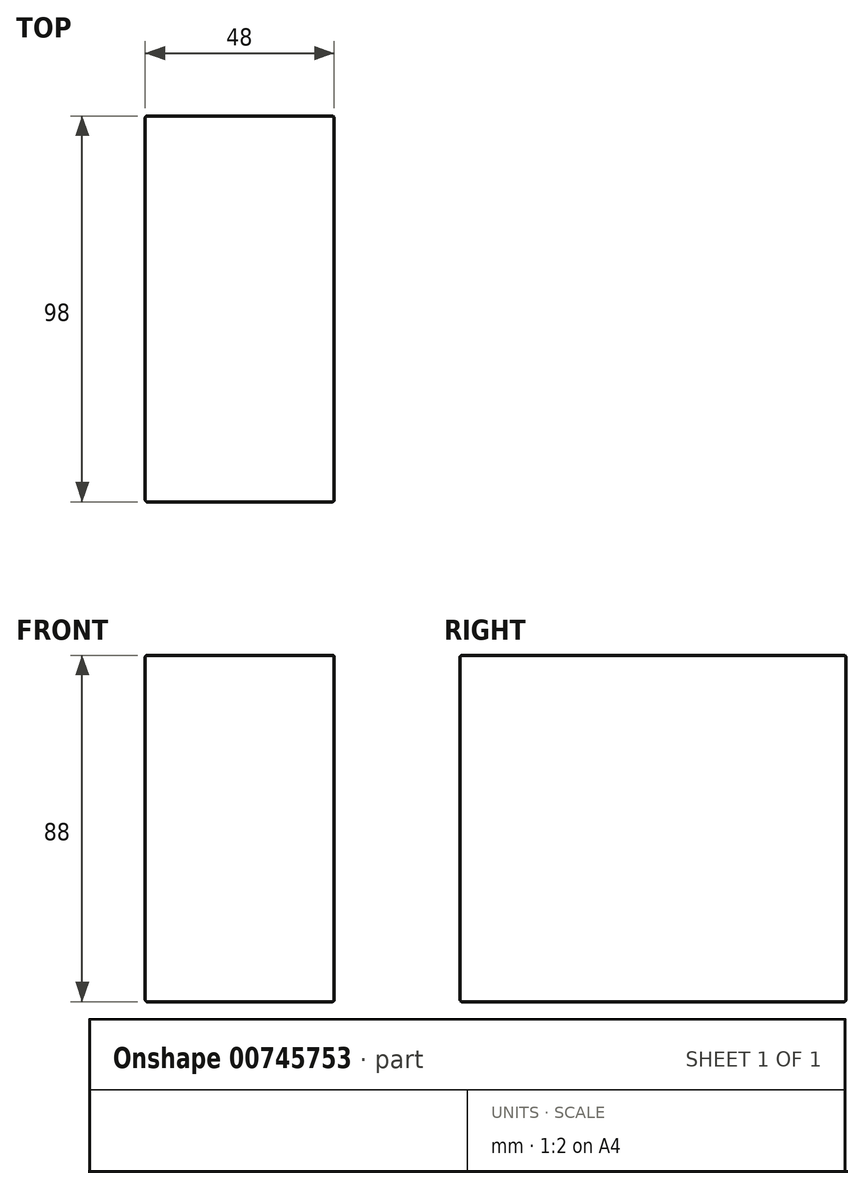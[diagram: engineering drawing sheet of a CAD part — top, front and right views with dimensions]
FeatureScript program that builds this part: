
annotation { "Feature Type Name" : "Feature", "Feature Type Description" : "" }
export const myFeature = defineFeature(function(context is Context, id is Id, definition is map)
    precondition{}
    {
        {
            var Q0;
            Q0=qCreatedBy(makeId("Front.planeOp"),FACE);
            var sketch = newSketch(context, id + "F0", { "sketchPlane" : qUnion([Q0])});
            skLineSegment(sketch, "E0.bottom", {"start": v(0, 0) * mm, "end": v(48, 0) * mm});
            skLineSegment(sketch, "E0.top", {"start": v(0, 88) * mm, "end": v(48, 88) * mm});
            skLineSegment(sketch, "E0.left", {"start": v(0, 0) * mm, "end": v(0, 88) * mm});
            skLineSegment(sketch, "E0.right", {"start": v(48, 0) * mm, "end": v(48, 88) * mm});
            skSolve(sketch);
        }
        {
            var Q0;
            Q0 = qSketchRegion(id + "F0", true);
            extrude(context, id + "F1", {"entities" : qUnion([Q0]), "oppositeDirection" : true, "depth" : 98 * mm, "offsetDistance" : 25 * mm});
        }
        {
            var Q0;
            Q0=makeQuery(id+"F1.opExtrude","CAP_EDGE",EDGE,{"disambiguationData":[OSD([sQuery(id+"F0.wireOp",EDGE,"E0.top")])],"isStart":true});
            var Q1;
            Q1=makeQuery(id+"F1.opExtrude","SWEPT_EDGE",EDGE,{"disambiguationData":[OSD([sQuery(id+"F0.wireOp",EDGE,"E0.top"),sQuery(id+"F0.wireOp",EDGE,"E0.right")])]});
            var Q2;
            Q2=makeQuery(id+"F1.opExtrude","CAP_EDGE",EDGE,{"disambiguationData":[OSD([sQuery(id+"F0.wireOp",EDGE,"E0.right")])],"isStart":true});
            var Q3;
            Q3=makeQuery(id+"F1.opExtrude","CAP_EDGE",EDGE,{"disambiguationData":[OSD([sQuery(id+"F0.wireOp",EDGE,"E0.left")])],"isStart":true});
            var Q4;
            Q4=makeQuery(id+"F1.opExtrude","SWEPT_EDGE",EDGE,{"disambiguationData":[OSD([sQuery(id+"F0.wireOp",EDGE,"E0.top"),sQuery(id+"F0.wireOp",EDGE,"E0.left")])]});
            var Q5;
            Q5=makeQuery(id+"F1.opExtrude","CAP_EDGE",EDGE,{"disambiguationData":[OSD([sQuery(id+"F0.wireOp",EDGE,"E0.top")])],"isStart":false});
            var Q6;
            Q6=makeQuery(id+"F1.opExtrude","CAP_EDGE",EDGE,{"disambiguationData":[OSD([sQuery(id+"F0.wireOp",EDGE,"E0.right")])],"isStart":false});
            var Q7;
            Q7=makeQuery(id+"F1.opExtrude","CAP_EDGE",EDGE,{"disambiguationData":[OSD([sQuery(id+"F0.wireOp",EDGE,"E0.left")])],"isStart":false});
            var Q8;
            Q8=makeQuery(id+"F1.opExtrude","SWEPT_EDGE",EDGE,{"disambiguationData":[OSD([sQuery(id+"F0.wireOp",EDGE,"E0.bottom"),sQuery(id+"F0.wireOp",EDGE,"E0.right")])]});
            var Q9;
            Q9=makeQuery(id+"F1.opExtrude","CAP_EDGE",EDGE,{"disambiguationData":[OSD([sQuery(id+"F0.wireOp",EDGE,"E0.bottom")])],"isStart":true});
            var Q10;
            Q10=makeQuery(id+"F1.opExtrude","CAP_EDGE",EDGE,{"disambiguationData":[OSD([sQuery(id+"F0.wireOp",EDGE,"E0.bottom")])],"isStart":false});
            var Q11;
            Q11=makeQuery(id+"F1.opExtrude","SWEPT_EDGE",EDGE,{"disambiguationData":[OSD([sQuery(id+"F0.wireOp",EDGE,"E0.bottom"),sQuery(id+"F0.wireOp",EDGE,"E0.left")])]});
            fillet(context, id + "F2", {"entities" : qUnion([Q0, Q1, Q2, Q3, Q4, Q5, Q6, Q7, Q8, Q9, Q10, Q11]), "radius" : 0.5 * mm, "tangentPropagation" : true, "allowEdgeOverflow" : false});
        }
    });
